# Revit family: BE_33683_de_DE
name_source: partatom
category: Leuchten
revit_build: Autodesk Revit 2015 (Build: 20150704_0715(x64)
units: mm (PartAtom-declared; Revit-internal decimal feet)

## types (4) — shared parameters
AC/DC = AC/DC
Aktualisierung = 2016-01-18T04:08:34
BEGA_Dummy = Nein
BEGA_IES = Ja
BEGA_Intern = Ja
BEGA_Intern_Konstruktion = Ja
BEGA_Intern_an = Ja
BEGA_Intern_aus = Ja
Befestigungsabstand = 220 mm
Befestigungsbohrung = Ø 5,5 mm
Beschreibung = Decken- und Wandleuchte
Beschreibung_Sonderanfertigung = Hier können Sie Informationen zur Sonderanfertigung eintragen.
CE_Konformität = ja
Energieeffizienzklasse = LED A++ - A
Farbfilter = 16777215
Farbtemperaturverschiebung bei Dämpfen der Lampe = <Keine Auswahl>
Farbwiedergabeindex = Ra > 80
Frequenz = 0/50-60 Hz
Gewicht = 3.55 kg
Hersteller = BEGA
Lampe = LED 26 W
Lastklassifizierung = Beleuchtung
Lebensdauerkriterien = L70 = 50.000 h
Logo = BEGA_Logo.png
M_W = Nein
Material_02 = BEGA_Oberfläche_Silber_matt
Material_11 = BEGA_Glas_opal
Neigungswinkel = 0.00°
Produktdatenblatt = http://www.bega.de
Scheinlast = 0 VA
Schutzart = IP 64
Schutzklasse = I
Sonderanfertigung = Nein
Spannung = 0 V
Typenbild = 33683.png
URL = http://www.bega.de
zero-valued in all types: Vorgabe-Ansicht

## per-type parameters (varying)
| type | Bestellnummer | Datei für fotometrisches Netz | Farbtemperatur | LED_Modulbezeichnung | Lampenlichtstrom | Leuchtenlichtstrom | M_A | M_G | Modell |
| BEGA_33683_Silber_K3 | 33683A | BE_33683.IES | 3000 K | LED-0451/830 | 2935 lm | 1896 lm | Ja | Nein | 33683A |
| BEGA_33683_Grafit_K3 | 33683 | BE_33683.IES | 3000 K | LED-0451/830 | 2935 lm | 1896 lm | Nein | Ja | 33683 |
| BEGA_33683_Silber_K4 | 33683AK4 | BE_33683K4.IES | 4000 K | LED-0451/840 | 3110 lm | 2009 lm | Ja | Nein | 33683AK4 |
| BEGA_33683_Grafit_K4 | 33683K4 | BE_33683K4.IES | 4000 K | LED-0451/840 | 3110 lm | 2009 lm | Nein | Ja | 33683K4 |
